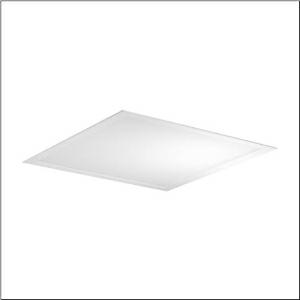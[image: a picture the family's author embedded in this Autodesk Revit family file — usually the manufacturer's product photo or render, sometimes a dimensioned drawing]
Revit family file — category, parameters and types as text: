
# Revit family: apollon_21_square_51mq11wd2614
name_source: partatom
category: Lighting Fixtures
units: mm (PartAtom-declared; Revit-internal decimal feet)

## family parameters
Cut with Voids When Loaded = No
Host = Face
Light Source = No
Part Type = Normal
Room Calculation Point = No
Round Connector Dimension = Use Diameter
Shared = No

## types (1)
- Apollon 21 square (1 x LED, 4150 lm, 24.7 W, 6500K)
    Apparent Load = 25 VA
    CIE Flux Codes = 60 87 97 100 100
    Color Rendering = 80
    Color Temperature = 6500K
    Default Elevation = 1800 mm
    Description = Apollon 21 square, office luminaire, primary optical cover: micro prismatic cover, of PMMA, CAT 2 (L<= 3000cd/m²), light emission: direct distribution, primary light characteristic: symmetric, installation type: lay-in mounting, LED, rated luminous flux: 4.150lm, luminous efficacy: 168lm/W, light colour: 865, colour temperature: 6500K, control gear: DALI 2, Multilumen, with terminal, 5-pole, mains connection: 220..240V, AC/DC, 0/50..60Hz, rated input power: 24.7W, housing, of aluminium, coated, traffic white (RAL 9016), module: M625, length: 620mm, width: 620mm, height: 55mm, recess depth: 180mm, housing upper side, of sheet steel, galvanised, protection rating (complete): IP20, protection rating (lamp compartment, on room side): IP50, insulation class (complete): insulation class II (safety insulation), certification: CE, ENEC, impact resistance: IK03, permissible operating ambient temperature: -20..+45°C, permissible storage temperature: -40..+80°C, standard: EN 60598-2-22, packaging unit: 1 piece
    Height = 0 mm  [stored 0 ft]
    Lamp = 1 x LED
    Lamp Light Flux = 4150 lm
    Lamp Power = 24.7 W
    Lamp count = 1
    Length = 620 mm
    Luminous efficacy = 168 lm/W
    Manufacturer = Siteco
    ModVariant = No
    Model = 51MQ11WD2614
    Mounting Place = Ceiling
    Mounting Type = Recessed
    Number of Poles = 1
    OnlyDefault = Yes
    Power Factor = 1
    Product Name = Apollon 21 square
    Product group = office luminaire | ceiling recessed
    ProductGroupID = 401
    Protection Class = Protection class II
    Protection Degree = IP 20
    RLX_Detail_Level = 1
    RLX_Emergency_Light_Flux = 0 lm
    RLX_Emergency_Type = 0
    RLX_Emergency_Type_DB = No
    RlxData = <blob elided: 13025 chars, md5=f2935f00>
    Socket = socket
    Standby Power = 0 W
    System Light Flux = 4150 lm
    System Power = 25 W
    Type Comments = Product without accessories
    Type Image = l_1291054.jpg
    URL = http://relux.com
    VarID = ---
    Voltage = 0 V
    Weight = 0.00 kg
    Width = 620 mm

note: [stored X ft] marks values corroborated as IEEE doubles in the binary element streams (Revit-internal decimal feet)

## geometry (parser evidence)
native form markers: Sweep x10
no freeform markers — native parametric forms only
